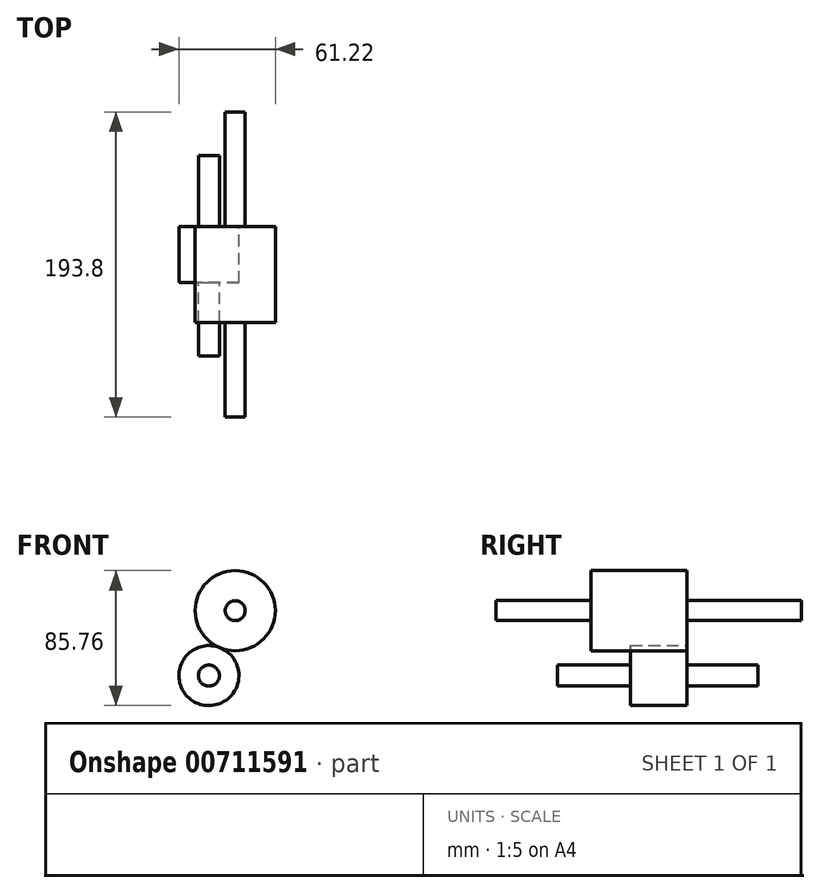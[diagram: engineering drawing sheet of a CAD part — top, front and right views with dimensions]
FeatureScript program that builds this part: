
annotation { "Feature Type Name" : "Feature", "Feature Type Description" : "" }
export const myFeature = defineFeature(function(context is Context, id is Id, definition is map)
    precondition{}
    {
        {
            var Q0;
            Q0=qCreatedBy(makeId("Front.planeOp"),FACE);
            var sketch = newSketch(context, id + "F0", { "sketchPlane" : qUnion([Q0])});
            skCircle(sketch, "E0", {"center": v(-45.41, 0) * mm, "radius": 19.05 * mm});
            skCircle(sketch, "E1", {"center": v(-28.7, 41.25) * mm, "radius": 6.35 * mm});
            skCircle(sketch, "E2", {"center": v(-45.41, 0) * mm, "radius": 6.66 * mm});
            skCircle(sketch, "E3", {"center": v(-28.7, 41.25) * mm, "radius": 25.46 * mm});
            skSolve(sketch);
        }
        {
            var Q0;
            Q0=makeQuery(id+"F0.imprint","IMPRINT",FACE,{"disambiguationData":[TD([[makeQuery(id+"F0.imprint","IMPRINT",EDGE,{"derivedFrom":sQuery(id+"F0.wireOp",EDGE,"E0")}),1.0]])]});
            var Q1;
            Q1=sQuery(id+"F0.wireOp",EDGE,"E0");
            extrude(context, id + "F1", {"entities" : qUnion([Q0]), "surfaceEntities" : qUnion([Q1]), "depth" : 35.81 * mm, "offsetDistance" : 25.4 * mm});
        }
        {
            var Q0;
            Q0=makeQuery(id+"F0.imprint","IMPRINT",FACE,{"disambiguationData":[TD([[makeQuery(id+"F0.imprint","IMPRINT",EDGE,{"derivedFrom":sQuery(id+"F0.wireOp",EDGE,"E1")}),-1.0]])]});
            extrude(context, id + "F2", {"entities" : qUnion([Q0]), "operationType" : NewBodyOperationType.ADD, "depth" : 60.96 * mm, "offsetDistance" : 25.4 * mm});
        }
        {
            var Q0;
            Q0=makeQuery(id+"F0.imprint","IMPRINT",FACE,{"disambiguationData":[TD([[makeQuery(id+"F0.imprint","IMPRINT",EDGE,{"derivedFrom":sQuery(id+"F0.wireOp",EDGE,"E1")}),1.0]])]});
            extrude(context, id + "F3", {"entities" : qUnion([Q0]), "operationType" : NewBodyOperationType.ADD, "depth" : 121.16 * mm, "offsetDistance" : 25.4 * mm, "hasSecondDirection" : true, "secondDirectionOppositeDirection" : true, "secondDirectionDepth" : 72.64 * mm});
        }
        {
            var Q0;
            Q0=makeQuery(id+"F0.imprint","IMPRINT",FACE,{"disambiguationData":[TD([[makeQuery(id+"F0.imprint","IMPRINT",EDGE,{"derivedFrom":sQuery(id+"F0.wireOp",EDGE,"E2")}),1.0]])]});
            var Q1;
            Q1=sQuery(id+"F0.wireOp",EDGE,"E2");
            extrude(context, id + "F4", {"entities" : qUnion([Q0]), "operationType" : NewBodyOperationType.ADD, "surfaceEntities" : qUnion([Q1]), "depth" : 82.3 * mm, "offsetDistance" : 25.4 * mm, "hasSecondDirection" : true, "secondDirectionOppositeDirection" : true, "secondDirectionDepth" : 44.96 * mm});
        }
    });
